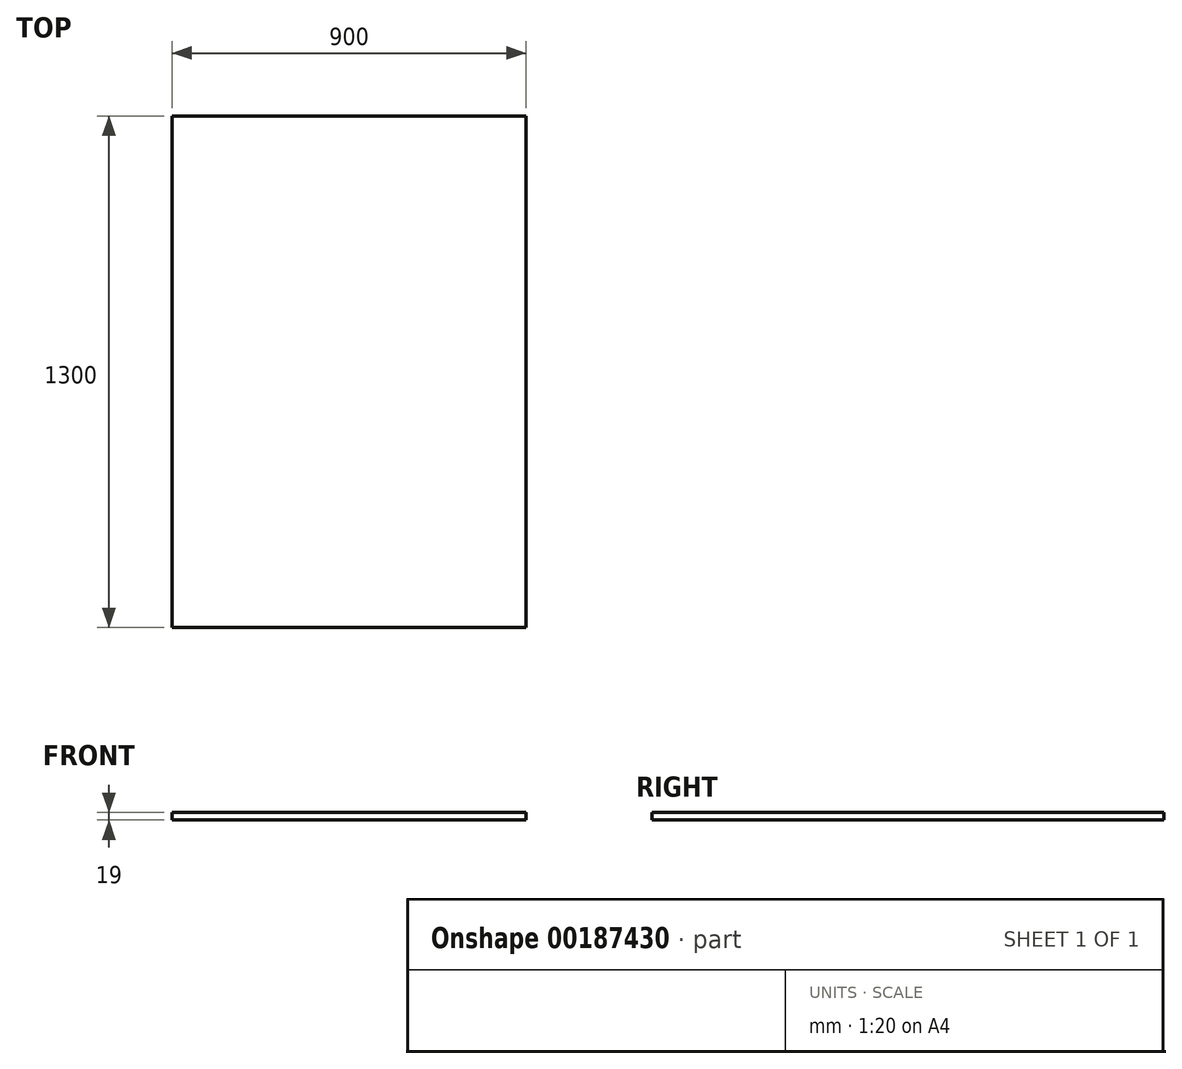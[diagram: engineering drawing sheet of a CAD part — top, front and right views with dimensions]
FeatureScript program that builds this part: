
annotation { "Feature Type Name" : "Feature", "Feature Type Description" : "" }
export const myFeature = defineFeature(function(context is Context, id is Id, definition is map)
    precondition{}
    {
        {
            var Q0;
            Q0=qCreatedBy(makeId("Top.planeOp"),FACE);
            var sketch = newSketch(context, id + "F0", { "sketchPlane" : qUnion([Q0])});
            skLineSegment(sketch, "E0.bottom", {"start": v(0, 0) * mm, "end": v(900, 0) * mm});
            skLineSegment(sketch, "E0.top", {"start": v(0, 1300) * mm, "end": v(900, 1300) * mm});
            skLineSegment(sketch, "E0.left", {"start": v(0, 0) * mm, "end": v(0, 1300) * mm});
            skLineSegment(sketch, "E0.right", {"start": v(900, 0) * mm, "end": v(900, 1300) * mm});
            skSolve(sketch);
        }
        {
            var Q0;
            Q0 = qSketchRegion(id + "F0", true);
            extrude(context, id + "F1", {"entities" : qUnion([Q0]), "depth" : 19 * mm});
        }
    });
